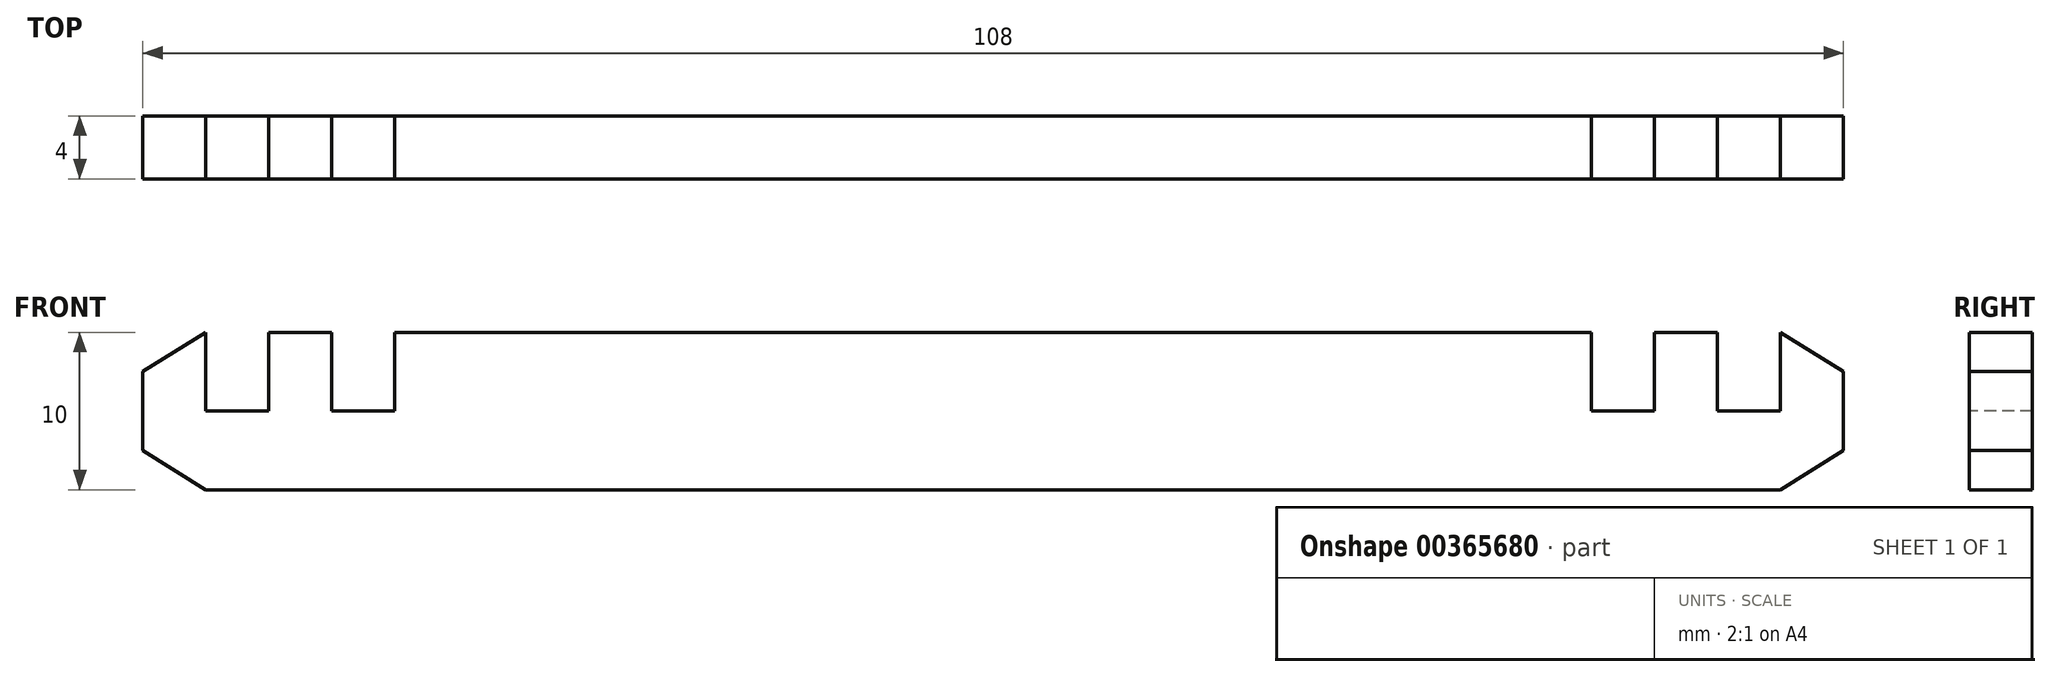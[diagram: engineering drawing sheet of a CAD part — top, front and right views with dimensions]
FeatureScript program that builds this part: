
annotation { "Feature Type Name" : "Feature", "Feature Type Description" : "" }
export const myFeature = defineFeature(function(context is Context, id is Id, definition is map)
    precondition{}
    {
        {
            var Q0;
            Q0=qCreatedBy(makeId("Front.planeOp"),FACE);
            var sketch = newSketch(context, id + "F0", { "sketchPlane" : qUnion([Q0])});
            skLineSegment(sketch, "E0", {"start": v(4, 0) * mm, "end": v(104, 0) * mm});
            skLineSegment(sketch, "E1", {"start": v(104, 10) * mm, "end": v(4, 10) * mm});
            skLineSegment(sketch, "E2", {"start": v(4, 10) * mm, "end": v(0, 7.5) * mm});
            skLineSegment(sketch, "E3", {"start": v(0, 7.5) * mm, "end": v(0, 2.5) * mm});
            skLineSegment(sketch, "E4", {"start": v(0, 2.5) * mm, "end": v(4, 0) * mm});
            skLineSegment(sketch, "E5", {"start": v(104, 10) * mm, "end": v(108, 7.5) * mm});
            skLineSegment(sketch, "E6", {"start": v(108, 7.5) * mm, "end": v(108, 2.5) * mm});
            skLineSegment(sketch, "E7", {"start": v(108, 2.5) * mm, "end": v(104, 0) * mm});
            skLineSegment(sketch, "E8", {"start": v(0, 2.5) * mm, "end": v(108, 2.5) * mm, "construction": true});
            skLineSegment(sketch, "E9", {"start": v(4, 0) * mm, "end": v(4, 10) * mm, "construction": true});
            skSolve(sketch);
        }
        {
            var Q0;
            Q0 = qSketchRegion(id + "F0", true);
            extrude(context, id + "F1", {"entities" : qUnion([Q0]), "depth" : 4 * mm});
        }
        {
            var Q0;
            Q0=makeQuery(id+"F1.opExtrude","CAP_FACE",FACE,{"disambiguationData":[OSD([sQuery(id+"F0.wireOp",EDGE,"E0"),sQuery(id+"F0.wireOp",EDGE,"E1"),sQuery(id+"F0.wireOp",EDGE,"E2"),sQuery(id+"F0.wireOp",EDGE,"E3"),sQuery(id+"F0.wireOp",EDGE,"E4"),sQuery(id+"F0.wireOp",EDGE,"E5"),sQuery(id+"F0.wireOp",EDGE,"E6"),sQuery(id+"F0.wireOp",EDGE,"E7")])],"isStart":false});
            var sketch = newSketch(context, id + "F2", { "sketchPlane" : qUnion([Q0])});
            skLineSegment(sketch, "E10.bottom", {"start": v(4, 10) * mm, "end": v(8, 10) * mm});
            skLineSegment(sketch, "E10.top", {"start": v(4, 5) * mm, "end": v(8, 5) * mm});
            skLineSegment(sketch, "E10.left", {"start": v(4, 10) * mm, "end": v(4, 5) * mm});
            skLineSegment(sketch, "E10.right", {"start": v(8, 10) * mm, "end": v(8, 5) * mm});
            skPoint(sketch, "E11.visualSharp", {"position": v(4, 5) * mm});
            skPoint(sketch, "E12.visualSharp", {"position": v(8, 5) * mm});
            skLineSegment(sketch, "E13", {"start": v(54, 10) * mm, "end": v(54, 0) * mm, "construction": true});
            skLineSegment(sketch, "E14.1.0.0", {"start": v(12, 10) * mm, "end": v(12, 5) * mm});
            skLineSegment(sketch, "E14.1.0.1", {"start": v(12, 10) * mm, "end": v(16, 10) * mm});
            skLineSegment(sketch, "E14.1.0.2", {"start": v(16, 10) * mm, "end": v(16, 5) * mm});
            skLineSegment(sketch, "E14.1.0.3", {"start": v(12, 5) * mm, "end": v(16, 5) * mm});
            skPoint(sketch, "E14.1.0.4", {"position": v(16, 5) * mm});
            skPoint(sketch, "E14.1.0.5", {"position": v(12, 5) * mm});
            skLineSegment(sketch, "E14.direction1", {"start": v(4, 5) * mm, "end": v(12, 5) * mm, "construction": true});
            skLineSegment(sketch, "E15.MirrorCS", {"start": v(104, 5) * mm, "end": v(100, 5) * mm});
            skLineSegment(sketch, "E16.MirrorCS", {"start": v(96, 5) * mm, "end": v(92, 5) * mm});
            skLineSegment(sketch, "E17.MirrorCS", {"start": v(104, 5) * mm, "end": v(96, 5) * mm, "construction": true});
            skLineSegment(sketch, "E18.MirrorCS", {"start": v(96, 10) * mm, "end": v(92, 10) * mm});
            skLineSegment(sketch, "E19.MirrorCS", {"start": v(100, 10) * mm, "end": v(100, 5) * mm});
            skLineSegment(sketch, "E20.MirrorCS", {"start": v(96, 10) * mm, "end": v(96, 5) * mm});
            skPoint(sketch, "E21.MirrorP", {"position": v(96, 5) * mm});
            skPoint(sketch, "E22.MirrorP", {"position": v(104, 5) * mm});
            skPoint(sketch, "E23.MirrorP", {"position": v(92, 5) * mm});
            skLineSegment(sketch, "E24.MirrorCS", {"start": v(104, 10) * mm, "end": v(100, 10) * mm});
            skLineSegment(sketch, "E25.MirrorCS", {"start": v(104, 10) * mm, "end": v(104, 5) * mm});
            skPoint(sketch, "E26.MirrorP", {"position": v(100, 5) * mm});
            skLineSegment(sketch, "E27.MirrorCS", {"start": v(92, 10) * mm, "end": v(92, 5) * mm});
            skSolve(sketch);
        }
        {
            var Q0;
            Q0 = qSketchRegion(id + "F2", true);
            extrude(context, id + "F3", {"entities" : qUnion([Q0]), "operationType" : NewBodyOperationType.REMOVE, "endBound" : BoundingType.UP_TO_NEXT, "oppositeDirection" : true, "depth" : 25 * mm});
        }
    });
